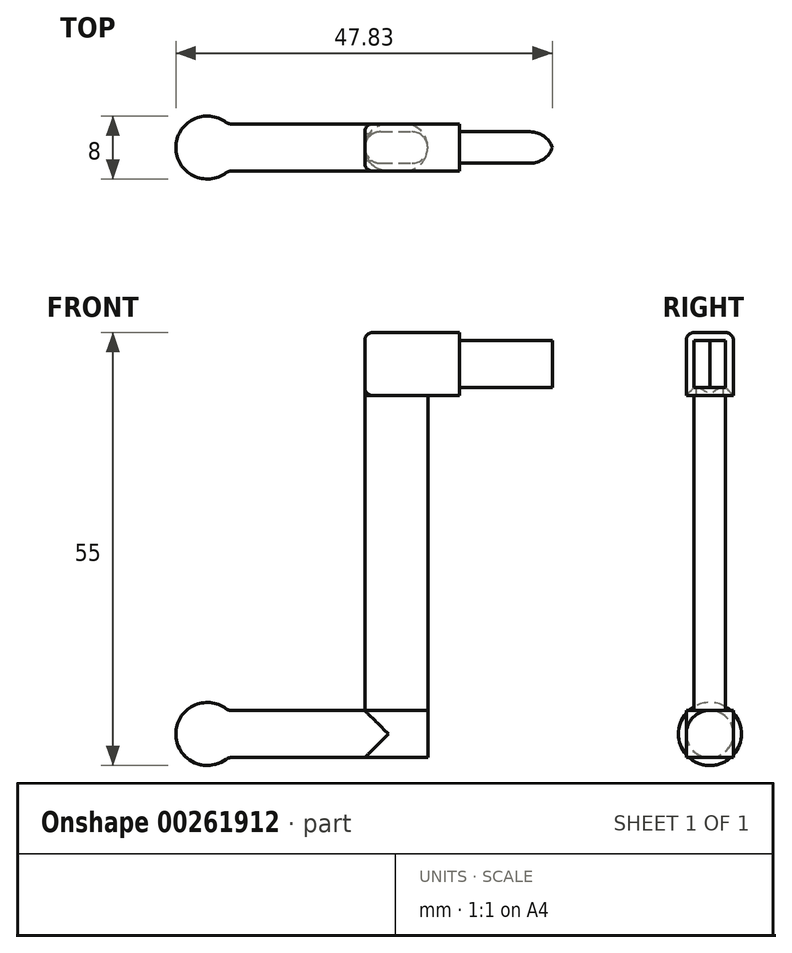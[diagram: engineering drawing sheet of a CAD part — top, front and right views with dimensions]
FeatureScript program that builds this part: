
annotation { "Feature Type Name" : "Feature", "Feature Type Description" : "" }
export const myFeature = defineFeature(function(context is Context, id is Id, definition is map)
    precondition{}
    {
        {
            var Q0;
            Q0=qCreatedBy(makeId("Right.planeOp"),FACE);
            var sketch = newSketch(context, id + "F0", { "sketchPlane" : qUnion([Q0])});
            skLineSegment(sketch, "E0.bottom", {"start": v(2, 3) * mm, "end": v(-2, 3) * mm});
            skLineSegment(sketch, "E0.top", {"start": v(2, -3) * mm, "end": v(-2, -3) * mm});
            skLineSegment(sketch, "E0.left", {"start": v(2, 3) * mm, "end": v(2, -3) * mm});
            skLineSegment(sketch, "E0.right", {"start": v(-2, 3) * mm, "end": v(-2, -3) * mm});
            skPoint(sketch, "E0.middle", {"position": v(0, 0) * mm});
            skSolve(sketch);
        }
        {
            var Q0;
            Q0=makeQuery(id+"F0.imprint","IMPRINT",FACE,{"disambiguationData":[TD([[makeQuery(id+"F0.imprint","IMPRINT",EDGE,{"derivedFrom":sQuery(id+"F0.wireOp",EDGE,"E0.bottom")}),1.0]])]});
            extrude(context, id + "F1", {"entities" : qUnion([Q0]), "oppositeDirection" : true, "depth" : 12 * mm});
        }
        {
            var Q0;
            Q0=makeQuery(id+"F1.opExtrude","CAP_FACE",FACE,{"disambiguationData":[OSD([sQuery(id+"F0.wireOp",EDGE,"E0.bottom"),sQuery(id+"F0.wireOp",EDGE,"E0.top"),sQuery(id+"F0.wireOp",EDGE,"E0.left"),sQuery(id+"F0.wireOp",EDGE,"E0.right")])],"isStart":false});
            var sketch = newSketch(context, id + "F2", { "sketchPlane" : qUnion([Q0])});
            skLineSegment(sketch, "E1.0", {"start": v(-3, 4) * mm, "end": v(-3, -4) * mm});
            skLineSegment(sketch, "E1.1", {"start": v(-3, 4) * mm, "end": v(3, 4) * mm});
            skLineSegment(sketch, "E1.2", {"start": v(3, 4) * mm, "end": v(3, -4) * mm});
            skLineSegment(sketch, "E1.3", {"start": v(-3, -4) * mm, "end": v(3, -4) * mm});
            skSolve(sketch);
        }
        {
            var Q0;
            Q0 = qSketchRegion(id + "F2", true);
            extrude(context, id + "F3", {"entities" : qUnion([Q0]), "operationType" : NewBodyOperationType.ADD, "depth" : 12 * mm});
        }
        {
            var Q0;
            Q0=makeQuery(id+"F3.opExtrude","SWEPT_FACE",FACE,{"disambiguationData":[OSD([sQuery(id+"F2.wireOp",EDGE,"E1.3")])]});
            var sketch = newSketch(context, id + "F4", { "sketchPlane" : qUnion([Q0])});
            skLineSegment(sketch, "E2.bottom", {"start": v(-22, -2) * mm, "end": v(-18, -2) * mm});
            skLineSegment(sketch, "E2.top", {"start": v(-22, 2) * mm, "end": v(-18, 2) * mm});
            skLineSegment(sketch, "E2.left", {"start": v(-24, 0) * mm, "end": v(-24, 0) * mm});
            skLineSegment(sketch, "E2.right", {"start": v(-16, 0) * mm, "end": v(-16, 0) * mm});
            skPoint(sketch, "E3", {"position": v(-24, 0) * mm});
            skPoint(sketch, "E4.visualSharp", {"position": v(-24, 2) * mm});
            skArc(sketch, "E4.filletArc", {"start": v(-22, 2) * mm, "mid": v(-23.41, 1.41) * mm, "end": v(-24, 0) * mm});
            skPoint(sketch, "E5.visualSharp", {"position": v(-24, -2) * mm});
            skArc(sketch, "E5.filletArc", {"start": v(-24, 0) * mm, "mid": v(-23.41, -1.41) * mm, "end": v(-22, -2) * mm});
            skPoint(sketch, "E6.visualSharp", {"position": v(-16, 2) * mm});
            skArc(sketch, "E6.filletArc", {"start": v(-16, 0) * mm, "mid": v(-16.59, 1.41) * mm, "end": v(-18, 2) * mm});
            skPoint(sketch, "E7.visualSharp", {"position": v(-16, -2) * mm});
            skArc(sketch, "E7.filletArc", {"start": v(-18, -2) * mm, "mid": v(-16.59, -1.41) * mm, "end": v(-16, 0) * mm});
            skSolve(sketch);
        }
        {
            var Q0;
            Q0 = qSketchRegion(id + "F4", true);
            extrude(context, id + "F5", {"entities" : qUnion([Q0]), "operationType" : NewBodyOperationType.ADD, "depth" : 40 * mm});
        }
        {
            var Q0;
            Q0=makeQuery(id+"F5.opExtrude","CAP_FACE",FACE,{"disambiguationData":[OSD([sQuery(id+"F4.wireOp",EDGE,"E2.bottom"),sQuery(id+"F4.wireOp",EDGE,"E2.top"),sQuery(id+"F4.wireOp",EDGE,"E4.filletArc"),sQuery(id+"F4.wireOp",EDGE,"E5.filletArc"),sQuery(id+"F4.wireOp",EDGE,"E6.filletArc"),sQuery(id+"F4.wireOp",EDGE,"E7.filletArc")])],"isStart":false});
            var sketch = newSketch(context, id + "F6", { "sketchPlane" : qUnion([Q0])});
            skLineSegment(sketch, "E8.0", {"start": v(-24, 3) * mm, "end": v(-16, 3) * mm});
            skLineSegment(sketch, "E9.0", {"start": v(-24, -3) * mm, "end": v(-16, -3) * mm});
            skLineSegment(sketch, "E10", {"start": v(-16, 3) * mm, "end": v(-16, -3) * mm});
            skPoint(sketch, "E10.startSnap0", {"position": v(-16, 0) * mm});
            skPoint(sketch, "E10.endSnap0", {"position": v(-16, 0) * mm});
            skPoint(sketch, "E11.orphan", {"position": v(-12, 3) * mm});
            skPoint(sketch, "E12.orphan", {"position": v(-12, -3) * mm});
            skLineSegment(sketch, "E13.0", {"start": v(-24, 0) * mm, "end": v(-24, 3) * mm});
            skLineSegment(sketch, "E14.0", {"start": v(-24, -3) * mm, "end": v(-24, 0) * mm});
            skSolve(sketch);
        }
        {
            var Q0;
            Q0 = qSketchRegion(id + "F6", true);
            extrude(context, id + "F7", {"entities" : qUnion([Q0]), "operationType" : NewBodyOperationType.ADD, "depth" : 6 * mm});
        }
        {
            var Q0;
            Q0=makeQuery(id+"F7.opExtrude","SWEPT_FACE",FACE,{"disambiguationData":[OSD([sQuery(id+"F6.wireOp",EDGE,"E13.0"),sQuery(id+"F6.wireOp",EDGE,"E14.0")])]});
            var sketch = newSketch(context, id + "F8", { "sketchPlane" : qUnion([Q0])});
            skCircle(sketch, "E15", {"center": v(0, -47) * mm, "radius": 3 * mm});
            skPoint(sketch, "E15.centerSnap0", {"position": v(3, -47) * mm});
            skSolve(sketch);
        }
        {
            var Q0;
            Q0 = qSketchRegion(id + "F8", true);
            extrude(context, id + "F9", {"entities" : qUnion([Q0]), "operationType" : NewBodyOperationType.ADD, "depth" : 20 * mm});
        }
        {
            var Q0;
            Q0=makeQuery(id+"F9.opExtrude","CAP_FACE",FACE,{"disambiguationData":[OSD([sQuery(id+"F8.wireOp",EDGE,"E15")])],"isStart":false});
            var sketch = newSketch(context, id + "F10", { "sketchPlane" : qUnion([Q0])});
            skCircle(sketch, "E16.0", {"center": v(0, -47) * mm, "radius": 4 * mm});
            skSolve(sketch);
        }
        {
            var Q0;
            Q0=qCreatedBy(makeId("Front.planeOp"),FACE);
            var sketch = newSketch(context, id + "F11", { "sketchPlane" : qUnion([Q0])});
            skLineSegment(sketch, "E17.0", {"start": v(-44, -47) * mm, "end": v(-44, -43) * mm});
            skArc(sketch, "E18", {"start": v(-40, -47) * mm, "mid": v(-44, -43) * mm, "end": v(-48, -47) * mm});
            skLineSegment(sketch, "E19", {"start": v(-48, -47) * mm, "end": v(-40, -47) * mm});
            skSolve(sketch);
        }
        {
            var Q0;
            Q0 = qSketchRegion(id + "F11", true);
            var Q1;
            Q1=sQuery(id+"F10.wireOp",EDGE,"E16.0");
            revolve(context, id + "F12", {"operationType" : NewBodyOperationType.ADD, "entities" : qUnion([Q0]), "axis" : qUnion([Q1]), "revolveType" : RevolveType.FULL});
        }
        {
            var Q0;
            Q0=makeQuery(id+"F1.opExtrude","CAP_EDGE",EDGE,{"disambiguationData":[OSD([sQuery(id+"F0.wireOp",EDGE,"E0.bottom")])],"isStart":false});
            var Q1;
            Q1=makeQuery(id+"F1.opExtrude","CAP_EDGE",EDGE,{"disambiguationData":[OSD([sQuery(id+"F0.wireOp",EDGE,"E0.left")])],"isStart":false});
            var Q2;
            Q2=makeQuery(id+"F1.opExtrude","CAP_EDGE",EDGE,{"disambiguationData":[OSD([sQuery(id+"F0.wireOp",EDGE,"E0.right")])],"isStart":false});
            var Q3;
            Q3=makeQuery(id+"F1.opExtrude","CAP_EDGE",EDGE,{"disambiguationData":[OSD([sQuery(id+"F0.wireOp",EDGE,"E0.top")])],"isStart":false});
            var Q4;
            Q4=makeQuery(id+"F1.opExtrude","CAP_EDGE",EDGE,{"disambiguationData":[OSD([sQuery(id+"F0.wireOp",EDGE,"E0.left")])],"isStart":true});
            var Q5;
            Q5=makeQuery(id+"F1.opExtrude","CAP_EDGE",EDGE,{"disambiguationData":[OSD([sQuery(id+"F0.wireOp",EDGE,"E0.right")])],"isStart":true});
            var Q6;
            Q6=makeQuery(id+"F7.opExtrude","SWEPT_EDGE",EDGE,{"disambiguationData":[OSD([sQuery(id+"F6.wireOp",EDGE,"E8.0"),sQuery(id+"F6.wireOp",EDGE,"E10")])]});
            var Q7;
            Q7=makeQuery(id+"F7.opExtrude","SWEPT_EDGE",EDGE,{"disambiguationData":[OSD([sQuery(id+"F6.wireOp",EDGE,"E9.0"),sQuery(id+"F6.wireOp",EDGE,"E10")])]});
            var Q8;
            {var subQ0=sQuery(id+"F6.wireOp",EDGE,"E8.0");var subQ1=sQuery(id+"F6.wireOp",EDGE,"E14.0");var subQ2=sQuery(id+"F6.wireOp",EDGE,"E13.0");Q8=makeQuery(id+"F9.boolean.opBoolean","SPLIT",EDGE,{"disambiguationData":[TD([makeQuery(id+"F7.opExtrude","CAP_FACE",FACE,{"disambiguationData":[OSD([subQ0,sQuery(id+"F6.wireOp",EDGE,"E9.0"),sQuery(id+"F6.wireOp",EDGE,"E10"),subQ2,subQ1])],"isStart":false})])],"derivedFrom":makeQuery(id+"F7.opExtrude","SWEPT_EDGE",EDGE,{"disambiguationData":[OSD([subQ0,subQ2])]})});}
            var Q9;
            {var subQ0=sQuery(id+"F6.wireOp",EDGE,"E14.0");var subQ1=sQuery(id+"F6.wireOp",EDGE,"E13.0");var subQ2=sQuery(id+"F6.wireOp",EDGE,"E9.0");Q9=makeQuery(id+"F9.boolean.opBoolean","SPLIT",EDGE,{"disambiguationData":[TD([makeQuery(id+"F7.opExtrude","CAP_FACE",FACE,{"disambiguationData":[OSD([sQuery(id+"F6.wireOp",EDGE,"E8.0"),subQ2,sQuery(id+"F6.wireOp",EDGE,"E10"),subQ1,subQ0])],"isStart":false})])],"derivedFrom":makeQuery(id+"F7.opExtrude","SWEPT_EDGE",EDGE,{"disambiguationData":[OSD([subQ2,subQ0])]})});}
            fillet(context, id + "F13", {"entities" : qUnion([Q0, Q1, Q2, Q3, Q4, Q5, Q6, Q7, Q8, Q9]), "radius" : 3 * mm, "tangentPropagation" : true, "allowEdgeOverflow" : false});
        }
        {
            var Q0;
            Q0=makeQuery(id+"F12.boolean.opBoolean","INTERSECT",EDGE,{"derivedFrom":[makeQuery(id+"F9.opExtrude","SWEPT_FACE",FACE,{"disambiguationData":[OSD([sQuery(id+"F8.wireOp",EDGE,"E15")])]}),makeQuery(id+"F12.opRevolve","SWEPT_FACE",FACE,{"disambiguationData":[OSD([sQuery(id+"F11.wireOp",EDGE,"E18")])]})]});
            var Q1;
            {var subQ0=sQuery(id+"F6.wireOp",EDGE,"E10");var subQ1=sQuery(id+"F6.wireOp",EDGE,"E9.0");Q1=makeQuery(id+"F13.opFillet","BLEND_EDGE",EDGE,{"blendedFrom":[makeQuery(id+"F7.opExtrude","SWEPT_EDGE",EDGE,{"disambiguationData":[OSD([subQ1,subQ0])]}),makeQuery(id+"F7.opExtrude","CAP_FACE",FACE,{"disambiguationData":[OSD([sQuery(id+"F6.wireOp",EDGE,"E8.0"),subQ1,subQ0,sQuery(id+"F6.wireOp",EDGE,"E13.0"),sQuery(id+"F6.wireOp",EDGE,"E14.0")])],"isStart":false})],"blendedInto":[makeQuery(id+"F7.opExtrude","CAP_FACE",FACE,{"disambiguationData":[OSD([sQuery(id+"F6.wireOp",EDGE,"E8.0"),subQ1,subQ0,sQuery(id+"F6.wireOp",EDGE,"E13.0"),sQuery(id+"F6.wireOp",EDGE,"E14.0")])],"isStart":false})]});}
            var Q2;
            Q2=makeQuery(id+"F3.opExtrude","SWEPT_EDGE",EDGE,{"disambiguationData":[OSD([sQuery(id+"F2.wireOp",EDGE,"E1.1"),sQuery(id+"F2.wireOp",EDGE,"E1.2")])]});
            var Q3;
            Q3=makeQuery(id+"F3.opExtrude","SWEPT_EDGE",EDGE,{"disambiguationData":[OSD([sQuery(id+"F2.wireOp",EDGE,"E1.0"),sQuery(id+"F2.wireOp",EDGE,"E1.1")])]});
            var Q4;
            Q4=makeQuery(id+"F3.opExtrude","CAP_EDGE",EDGE,{"disambiguationData":[OSD([sQuery(id+"F2.wireOp",EDGE,"E1.1")])],"isStart":false});
            var Q5;
            Q5=makeQuery(id+"F13.opFillet","BLEND_EDGE",EDGE,{"blendedFrom":[makeQuery(id+"F1.opExtrude","CAP_EDGE",EDGE,{"disambiguationData":[OSD([sQuery(id+"F0.wireOp",EDGE,"E0.bottom")])],"isStart":false}),makeQuery(id+"F3.opExtrude","SWEPT_FACE",FACE,{"disambiguationData":[OSD([sQuery(id+"F2.wireOp",EDGE,"E1.1")])]})],"blendedInto":[makeQuery(id+"F3.opExtrude","SWEPT_FACE",FACE,{"disambiguationData":[OSD([sQuery(id+"F2.wireOp",EDGE,"E1.1")])]})]});
            var Q6;
            Q6=makeQuery(id+"F3.opExtrude","CAP_FACE",FACE,{"disambiguationData":[OSD([sQuery(id+"F2.wireOp",EDGE,"E1.0"),sQuery(id+"F2.wireOp",EDGE,"E1.1"),sQuery(id+"F2.wireOp",EDGE,"E1.2"),sQuery(id+"F2.wireOp",EDGE,"E1.3")])],"isStart":false});
            var Q7;
            Q7=makeQuery(id+"F13.opFillet","BLEND_EDGE",EDGE,{"blendedFrom":[makeQuery(id+"F1.opExtrude","CAP_EDGE",EDGE,{"disambiguationData":[OSD([sQuery(id+"F0.wireOp",EDGE,"E0.top")])],"isStart":false}),makeQuery(id+"F3.opExtrude","SWEPT_FACE",FACE,{"disambiguationData":[OSD([sQuery(id+"F2.wireOp",EDGE,"E1.3")])]})],"blendedInto":[makeQuery(id+"F3.opExtrude","SWEPT_FACE",FACE,{"disambiguationData":[OSD([sQuery(id+"F2.wireOp",EDGE,"E1.3")])]})]});
            fillet(context, id + "F14", {"entities" : qUnion([Q0, Q1, Q2, Q3, Q4, Q5, Q6, Q7]), "radius" : 1 * mm, "tangentPropagation" : true, "allowEdgeOverflow" : false});
        }
    });
